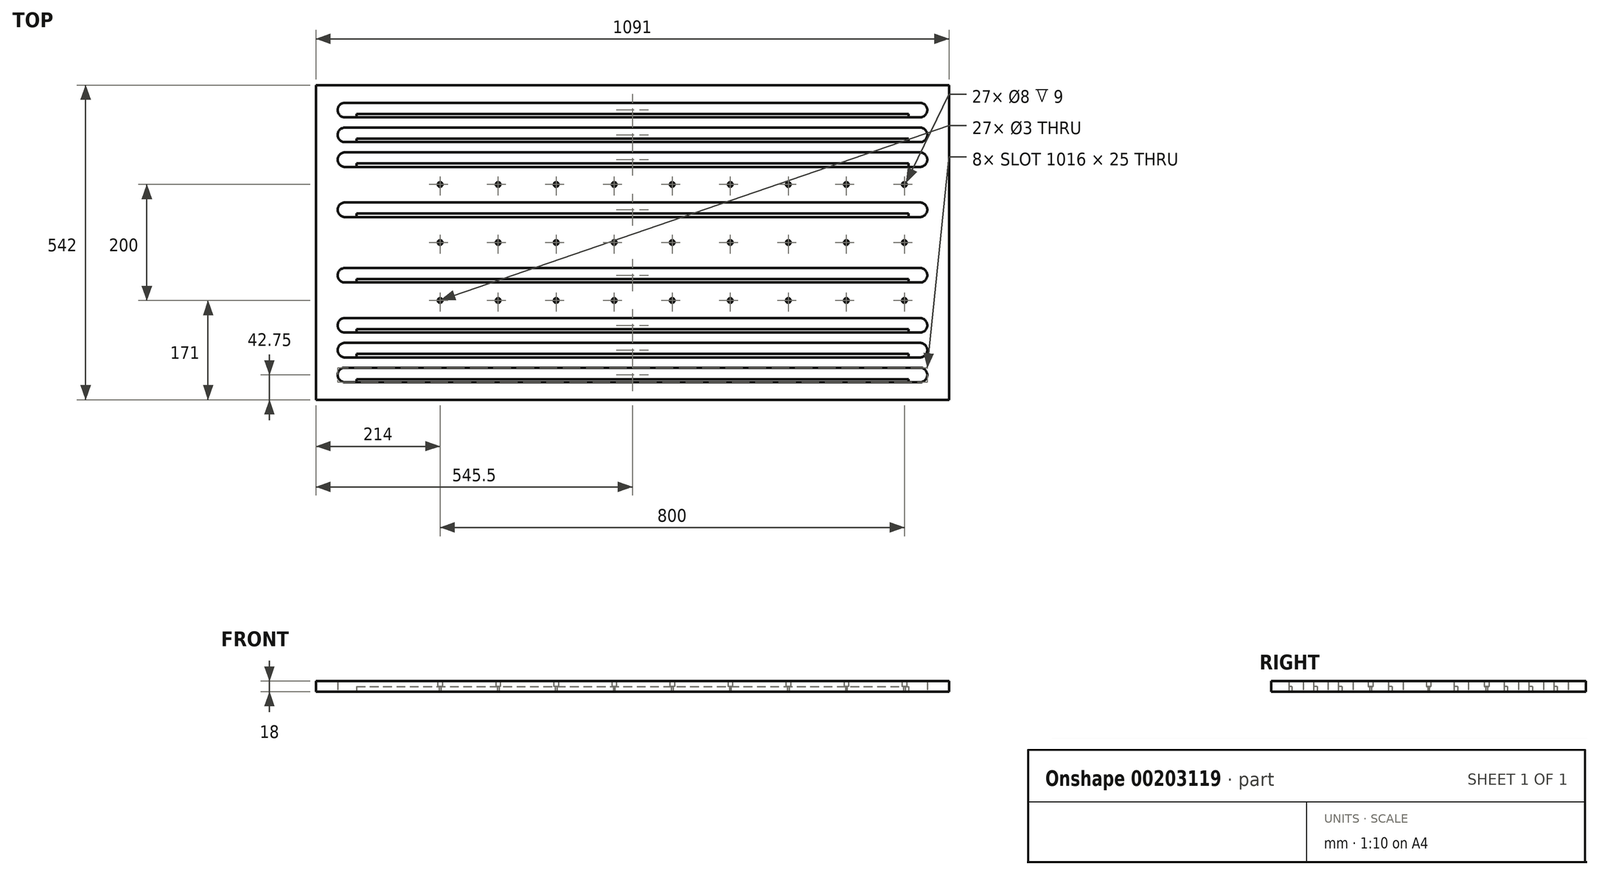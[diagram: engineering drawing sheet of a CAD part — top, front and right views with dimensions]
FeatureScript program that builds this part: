
annotation { "Feature Type Name" : "Feature", "Feature Type Description" : "" }
export const myFeature = defineFeature(function(context is Context, id is Id, definition is map)
    precondition{}
    {
        {
            var Q0;
            Q0=qCreatedBy(makeId("Top.planeOp"),FACE);
            var sketch = newSketch(context, id + "F0", { "sketchPlane" : qUnion([Q0])});
            skLineSegment(sketch, "E0.bottom", {"start": v(0, 0) * mm, "end": v(1091, 0) * mm});
            skLineSegment(sketch, "E0.top", {"start": v(0, 542) * mm, "end": v(1091, 542) * mm});
            skLineSegment(sketch, "E0.left", {"start": v(0, 0) * mm, "end": v(0, 542) * mm});
            skLineSegment(sketch, "E0.right", {"start": v(1091, 0) * mm, "end": v(1091, 542) * mm});
            skPoint(sketch, "E1", {"position": v(214, 171) * mm});
            skPoint(sketch, "E2", {"position": v(214, 271) * mm});
            skPoint(sketch, "E3", {"position": v(214, 371) * mm});
            skLineSegment(sketch, "E4", {"start": v(-315.3, 371) * mm, "end": v(-315.3, 271) * mm, "construction": true});
            skLineSegment(sketch, "E5", {"start": v(-315.3, 271) * mm, "end": v(-315.3, 171) * mm, "construction": true});
            skLineSegment(sketch, "E6", {"start": v(-315.3, 171) * mm, "end": v(-315.3, 0) * mm, "construction": true});
            skLineSegment(sketch, "E7", {"start": v(-315.3, 542) * mm, "end": v(-315.3, 371) * mm, "construction": true});
            skPoint(sketch, "E8", {"position": v(-315.3, 456.5) * mm});
            skPoint(sketch, "E9", {"position": v(-315.3, 327.44) * mm});
            skPoint(sketch, "E10", {"position": v(-315.3, 221) * mm});
            skPoint(sketch, "E11", {"position": v(-315.3, 85.5) * mm});
            skLineSegment(sketch, "E12", {"start": v(50, 327.44) * mm, "end": v(1041, 327.44) * mm, "construction": true});
            skLineSegment(sketch, "E13", {"start": v(50, 456.5) * mm, "end": v(1041, 456.5) * mm, "construction": true});
            skLineSegment(sketch, "E14", {"start": v(1046.67, 271) * mm, "end": v(1429.51, 271) * mm, "construction": true});
            skPoint(sketch, "E14.endSnap0", {"position": v(1091, 271) * mm});
            skLineSegment(sketch, "E15", {"start": v(-218.04, 542) * mm, "end": v(-218.04, 456.5) * mm, "construction": true});
            skPoint(sketch, "E16", {"position": v(-218.04, 499.25) * mm});
            skLineSegment(sketch, "E17", {"start": v(50, 499.25) * mm, "end": v(1041, 499.25) * mm, "construction": true});
            skLineSegment(sketch, "E18", {"start": v(-218.04, 456.5) * mm, "end": v(-218.04, 371) * mm, "construction": true});
            skPoint(sketch, "E19", {"position": v(-218.04, 413.75) * mm});
            skLineSegment(sketch, "E20", {"start": v(50, 413.75) * mm, "end": v(1041, 413.75) * mm, "construction": true});
            skLineSegment(sketch, "E21.MirrorCS", {"start": v(50, 42.75) * mm, "end": v(1041, 42.75) * mm, "construction": true});
            skLineSegment(sketch, "E22.MirrorCS", {"start": v(50, 85.5) * mm, "end": v(1041, 85.5) * mm, "construction": true});
            skLineSegment(sketch, "E23.MirrorCS", {"start": v(50, 128.25) * mm, "end": v(1041, 128.25) * mm, "construction": true});
            skLineSegment(sketch, "E24.MirrorCS", {"start": v(50, 214.56) * mm, "end": v(1041, 214.56) * mm, "construction": true});
            skSolve(sketch);
        }
        {
            var Q0;
            Q0=makeQuery(id+"F0.imprint","IMPRINT",FACE,{"disambiguationData":[TD([[makeQuery(id+"F0.imprint","IMPRINT",EDGE,{"derivedFrom":sQuery(id+"F0.wireOp",EDGE,"E0.bottom")}),1.0]])]});
            var sketch = newSketch(context, id + "F1", { "sketchPlane" : qUnion([Q0])});
            skLineSegment(sketch, "E25.bottom", {"start": v(0, 0) * mm, "end": v(1091, 0) * mm});
            skLineSegment(sketch, "E25.top", {"start": v(0, 542) * mm, "end": v(1091, 542) * mm});
            skLineSegment(sketch, "E25.left", {"start": v(0, 0) * mm, "end": v(0, 542) * mm});
            skLineSegment(sketch, "E25.right", {"start": v(1091, 0) * mm, "end": v(1091, 542) * mm});
            skLineSegment(sketch, "E26.JFx.JFx", {"start": v(50, 499.25) * mm, "end": v(1041, 499.25) * mm, "construction": true});
            skLineSegment(sketch, "E26.JFl.JFl", {"start": v(50, 456.5) * mm, "end": v(1041, 456.5) * mm, "construction": true});
            skLineSegment(sketch, "E26.JF5.JF5", {"start": v(50, 413.75) * mm, "end": v(1041, 413.75) * mm, "construction": true});
            skLineSegment(sketch, "E26.JFh.JFh", {"start": v(50, 327.44) * mm, "end": v(1041, 327.44) * mm, "construction": true});
            skLineSegment(sketch, "E26.KFJB.KFJB", {"start": v(50, 214.56) * mm, "end": v(1041, 214.56) * mm, "construction": true});
            skLineSegment(sketch, "E26.KFFB.KFFB", {"start": v(50, 128.25) * mm, "end": v(1041, 128.25) * mm, "construction": true});
            skLineSegment(sketch, "E26.KFBB.KFBB", {"start": v(50, 85.5) * mm, "end": v(1041, 85.5) * mm, "construction": true});
            skLineSegment(sketch, "E26.JF9.JF9", {"start": v(50, 42.75) * mm, "end": v(1041, 42.75) * mm, "construction": true});
            skArc(sketch, "E26.0.startCap", {"start": v(50, 486.75) * mm, "mid": v(37.5, 499.25) * mm, "end": v(50, 511.75) * mm});
            skArc(sketch, "E26.0.endCap", {"start": v(1041, 511.75) * mm, "mid": v(1053.5, 499.25) * mm, "end": v(1041, 486.75) * mm});
            skLineSegment(sketch, "E26.0.left", {"start": v(50, 511.75) * mm, "end": v(1041, 511.75) * mm});
            skLineSegment(sketch, "E26.0.right", {"start": v(50, 486.75) * mm, "end": v(1041, 486.75) * mm});
            skArc(sketch, "E26.1.startCap", {"start": v(50, 444) * mm, "mid": v(37.5, 456.5) * mm, "end": v(50, 469) * mm});
            skArc(sketch, "E26.1.endCap", {"start": v(1041, 469) * mm, "mid": v(1053.5, 456.5) * mm, "end": v(1041, 444) * mm});
            skLineSegment(sketch, "E26.1.left", {"start": v(50, 469) * mm, "end": v(1041, 469) * mm});
            skLineSegment(sketch, "E26.1.right", {"start": v(50, 444) * mm, "end": v(1041, 444) * mm});
            skArc(sketch, "E26.2.startCap", {"start": v(50, 401.25) * mm, "mid": v(37.5, 413.75) * mm, "end": v(50, 426.25) * mm});
            skArc(sketch, "E26.2.endCap", {"start": v(1041, 426.25) * mm, "mid": v(1053.5, 413.75) * mm, "end": v(1041, 401.25) * mm});
            skLineSegment(sketch, "E26.2.left", {"start": v(50, 426.25) * mm, "end": v(1041, 426.25) * mm});
            skLineSegment(sketch, "E26.2.right", {"start": v(50, 401.25) * mm, "end": v(1041, 401.25) * mm});
            skArc(sketch, "E26.3.startCap", {"start": v(50, 314.94) * mm, "mid": v(37.5, 327.44) * mm, "end": v(50, 339.94) * mm});
            skArc(sketch, "E26.3.endCap", {"start": v(1041, 339.94) * mm, "mid": v(1053.5, 327.44) * mm, "end": v(1041, 314.94) * mm});
            skLineSegment(sketch, "E26.3.left", {"start": v(50, 339.94) * mm, "end": v(1041, 339.94) * mm});
            skLineSegment(sketch, "E26.3.right", {"start": v(50, 314.94) * mm, "end": v(1041, 314.94) * mm});
            skArc(sketch, "E26.4.startCap", {"start": v(50, 202.06) * mm, "mid": v(37.5, 214.56) * mm, "end": v(50, 227.06) * mm});
            skArc(sketch, "E26.4.endCap", {"start": v(1041, 227.06) * mm, "mid": v(1053.5, 214.56) * mm, "end": v(1041, 202.06) * mm});
            skLineSegment(sketch, "E26.4.left", {"start": v(50, 227.06) * mm, "end": v(1041, 227.06) * mm});
            skLineSegment(sketch, "E26.4.right", {"start": v(50, 202.06) * mm, "end": v(1041, 202.06) * mm});
            skArc(sketch, "E26.5.startCap", {"start": v(50, 115.75) * mm, "mid": v(37.5, 128.25) * mm, "end": v(50, 140.75) * mm});
            skArc(sketch, "E26.5.endCap", {"start": v(1041, 140.75) * mm, "mid": v(1053.5, 128.25) * mm, "end": v(1041, 115.75) * mm});
            skLineSegment(sketch, "E26.5.left", {"start": v(50, 140.75) * mm, "end": v(1041, 140.75) * mm});
            skLineSegment(sketch, "E26.5.right", {"start": v(50, 115.75) * mm, "end": v(1041, 115.75) * mm});
            skArc(sketch, "E26.6.startCap", {"start": v(50, 73) * mm, "mid": v(37.5, 85.5) * mm, "end": v(50, 98) * mm});
            skArc(sketch, "E26.6.endCap", {"start": v(1041, 98) * mm, "mid": v(1053.5, 85.5) * mm, "end": v(1041, 73) * mm});
            skLineSegment(sketch, "E26.6.left", {"start": v(50, 98) * mm, "end": v(1041, 98) * mm});
            skLineSegment(sketch, "E26.6.right", {"start": v(50, 73) * mm, "end": v(1041, 73) * mm});
            skArc(sketch, "E26.7.startCap", {"start": v(50, 30.25) * mm, "mid": v(37.5, 42.75) * mm, "end": v(50, 55.25) * mm});
            skArc(sketch, "E26.7.endCap", {"start": v(1041, 55.25) * mm, "mid": v(1053.5, 42.75) * mm, "end": v(1041, 30.25) * mm});
            skLineSegment(sketch, "E26.7.left", {"start": v(50, 55.25) * mm, "end": v(1041, 55.25) * mm});
            skLineSegment(sketch, "E26.7.right", {"start": v(50, 30.25) * mm, "end": v(1041, 30.25) * mm});
            skPoint(sketch, "E27", {"position": v(545.5, 511.75) * mm});
            skLineSegment(sketch, "E28.bottom", {"start": v(70, 511.75) * mm, "end": v(1021, 511.75) * mm});
            skLineSegment(sketch, "E28.top", {"start": v(70, 505.75) * mm, "end": v(1021, 505.75) * mm});
            skLineSegment(sketch, "E28.left", {"start": v(70, 511.75) * mm, "end": v(70, 505.75) * mm});
            skLineSegment(sketch, "E28.right", {"start": v(1021, 511.75) * mm, "end": v(1021, 505.75) * mm});
            skLineSegment(sketch, "E29.bottom", {"start": v(70, 492.75) * mm, "end": v(1021, 492.75) * mm});
            skLineSegment(sketch, "E29.top", {"start": v(70, 486.75) * mm, "end": v(1021, 486.75) * mm});
            skLineSegment(sketch, "E29.left", {"start": v(70, 492.75) * mm, "end": v(70, 486.75) * mm});
            skLineSegment(sketch, "E29.right", {"start": v(1021, 492.75) * mm, "end": v(1021, 486.75) * mm});
            skLineSegment(sketch, "E30.bottom", {"start": v(70, 98) * mm, "end": v(1021, 98) * mm});
            skLineSegment(sketch, "E30.top", {"start": v(70, 92) * mm, "end": v(1021, 92) * mm});
            skLineSegment(sketch, "E30.left", {"start": v(1021, 98) * mm, "end": v(1021, 92) * mm});
            skLineSegment(sketch, "E30.right", {"start": v(70, 98) * mm, "end": v(70, 92) * mm});
            skPoint(sketch, "E31", {"position": v(545.5, 98) * mm});
            skLineSegment(sketch, "E32.bottom", {"start": v(70, 79) * mm, "end": v(1021, 79) * mm});
            skLineSegment(sketch, "E32.top", {"start": v(70, 73) * mm, "end": v(1021, 73) * mm});
            skLineSegment(sketch, "E32.left", {"start": v(1021, 79) * mm, "end": v(1021, 73) * mm});
            skLineSegment(sketch, "E32.right", {"start": v(70, 79) * mm, "end": v(70, 73) * mm});
            skLineSegment(sketch, "E33.bottom", {"start": v(70, 426.25) * mm, "end": v(1021, 426.25) * mm});
            skLineSegment(sketch, "E33.top", {"start": v(70, 420.25) * mm, "end": v(1021, 420.25) * mm});
            skLineSegment(sketch, "E33.left", {"start": v(1021, 426.25) * mm, "end": v(1021, 420.25) * mm});
            skLineSegment(sketch, "E33.right", {"start": v(70, 426.25) * mm, "end": v(70, 420.25) * mm});
            skPoint(sketch, "E34", {"position": v(545.5, 426.25) * mm});
            skLineSegment(sketch, "E35.bottom", {"start": v(70, 407.25) * mm, "end": v(1021, 407.25) * mm});
            skLineSegment(sketch, "E35.top", {"start": v(70, 401.25) * mm, "end": v(1021, 401.25) * mm});
            skLineSegment(sketch, "E35.left", {"start": v(1021, 407.25) * mm, "end": v(1021, 401.25) * mm});
            skLineSegment(sketch, "E35.right", {"start": v(70, 407.25) * mm, "end": v(70, 401.25) * mm});
            skLineSegment(sketch, "E36.bottom", {"start": v(70, 469) * mm, "end": v(1021, 469) * mm});
            skLineSegment(sketch, "E36.top", {"start": v(70, 463) * mm, "end": v(1021, 463) * mm});
            skLineSegment(sketch, "E36.left", {"start": v(1021, 469) * mm, "end": v(1021, 463) * mm});
            skLineSegment(sketch, "E36.right", {"start": v(70, 469) * mm, "end": v(70, 463) * mm});
            skPoint(sketch, "E37", {"position": v(545.5, 469) * mm});
            skLineSegment(sketch, "E38.bottom", {"start": v(70, 450) * mm, "end": v(1021, 450) * mm});
            skLineSegment(sketch, "E38.top", {"start": v(70, 444) * mm, "end": v(1021, 444) * mm});
            skLineSegment(sketch, "E38.left", {"start": v(1021, 450) * mm, "end": v(1021, 444) * mm});
            skLineSegment(sketch, "E38.right", {"start": v(70, 450) * mm, "end": v(70, 444) * mm});
            skPoint(sketch, "E39", {"position": v(545.5, 339.94) * mm});
            skPoint(sketch, "E40", {"position": v(545.5, 227.06) * mm});
            skPoint(sketch, "E41", {"position": v(545.5, 140.75) * mm});
            skPoint(sketch, "E42", {"position": v(545.5, 55.25) * mm});
            skLineSegment(sketch, "E43.bottom", {"start": v(70, 140.75) * mm, "end": v(1021, 140.75) * mm});
            skLineSegment(sketch, "E43.top", {"start": v(70, 134.75) * mm, "end": v(1021, 134.75) * mm});
            skLineSegment(sketch, "E43.left", {"start": v(70, 140.75) * mm, "end": v(70, 134.75) * mm});
            skLineSegment(sketch, "E43.right", {"start": v(1021, 140.75) * mm, "end": v(1021, 134.75) * mm});
            skLineSegment(sketch, "E44.bottom", {"start": v(70, 121.75) * mm, "end": v(1021, 121.75) * mm});
            skLineSegment(sketch, "E44.top", {"start": v(70, 115.75) * mm, "end": v(1021, 115.75) * mm});
            skLineSegment(sketch, "E44.left", {"start": v(70, 121.75) * mm, "end": v(70, 115.75) * mm});
            skLineSegment(sketch, "E44.right", {"start": v(1021, 121.75) * mm, "end": v(1021, 115.75) * mm});
            skLineSegment(sketch, "E45.bottom", {"start": v(70, 55.25) * mm, "end": v(1021, 55.25) * mm});
            skLineSegment(sketch, "E45.top", {"start": v(70, 50.25) * mm, "end": v(1021, 50.25) * mm});
            skLineSegment(sketch, "E45.left", {"start": v(70, 55.25) * mm, "end": v(70, 50.25) * mm});
            skLineSegment(sketch, "E45.right", {"start": v(1021, 55.25) * mm, "end": v(1021, 50.25) * mm});
            skLineSegment(sketch, "E46.bottom", {"start": v(70, 35.25) * mm, "end": v(1021, 35.25) * mm});
            skLineSegment(sketch, "E46.top", {"start": v(70, 30.25) * mm, "end": v(1021, 30.25) * mm});
            skLineSegment(sketch, "E46.left", {"start": v(70, 35.25) * mm, "end": v(70, 30.25) * mm});
            skLineSegment(sketch, "E46.right", {"start": v(1021, 35.25) * mm, "end": v(1021, 30.25) * mm});
            skLineSegment(sketch, "E47.bottom", {"start": v(70, 227.06) * mm, "end": v(1021, 227.06) * mm});
            skLineSegment(sketch, "E47.top", {"start": v(70, 221.06) * mm, "end": v(1021, 221.06) * mm});
            skLineSegment(sketch, "E47.left", {"start": v(70, 227.06) * mm, "end": v(70, 221.06) * mm});
            skLineSegment(sketch, "E47.right", {"start": v(1021, 227.06) * mm, "end": v(1021, 221.06) * mm});
            skLineSegment(sketch, "E48.bottom", {"start": v(70, 208.06) * mm, "end": v(1021, 208.06) * mm});
            skLineSegment(sketch, "E48.top", {"start": v(70, 202.06) * mm, "end": v(1021, 202.06) * mm});
            skLineSegment(sketch, "E48.left", {"start": v(70, 208.06) * mm, "end": v(70, 202.06) * mm});
            skLineSegment(sketch, "E48.right", {"start": v(1021, 208.06) * mm, "end": v(1021, 202.06) * mm});
            skPoint(sketch, "E49", {"position": v(545.5, 30.25) * mm});
            skLineSegment(sketch, "E50.bottom", {"start": v(70, 339.94) * mm, "end": v(1021, 339.94) * mm});
            skLineSegment(sketch, "E50.top", {"start": v(70, 333.94) * mm, "end": v(1021, 333.94) * mm});
            skLineSegment(sketch, "E50.left", {"start": v(70, 339.94) * mm, "end": v(70, 333.94) * mm});
            skLineSegment(sketch, "E50.right", {"start": v(1021, 339.94) * mm, "end": v(1021, 333.94) * mm});
            skLineSegment(sketch, "E51.bottom", {"start": v(70, 320.94) * mm, "end": v(1021, 320.94) * mm});
            skLineSegment(sketch, "E51.top", {"start": v(70, 314.94) * mm, "end": v(1021, 314.94) * mm});
            skLineSegment(sketch, "E51.left", {"start": v(70, 320.94) * mm, "end": v(70, 314.94) * mm});
            skLineSegment(sketch, "E51.right", {"start": v(1021, 320.94) * mm, "end": v(1021, 314.94) * mm});
            skPoint(sketch, "E52", {"position": v(545.5, 214.56) * mm});
            skCircle(sketch, "E53", {"center": v(214, 171) * mm, "radius": 4 * mm});
            skCircle(sketch, "E54", {"center": v(214, 171) * mm, "radius": 1.5 * mm});
            skCircle(sketch, "E55.0.1.0", {"center": v(214, 271) * mm, "radius": 4 * mm});
            skCircle(sketch, "E55.0.1.1", {"center": v(214, 271) * mm, "radius": 1.5 * mm});
            skCircle(sketch, "E55.0.2.0", {"center": v(214, 371) * mm, "radius": 4 * mm});
            skCircle(sketch, "E55.0.2.1", {"center": v(214, 371) * mm, "radius": 1.5 * mm});
            skCircle(sketch, "E55.1.0.0", {"center": v(314, 171) * mm, "radius": 4 * mm});
            skCircle(sketch, "E55.1.0.1", {"center": v(314, 171) * mm, "radius": 1.5 * mm});
            skCircle(sketch, "E55.1.1.0", {"center": v(314, 271) * mm, "radius": 4 * mm});
            skCircle(sketch, "E55.1.1.1", {"center": v(314, 271) * mm, "radius": 1.5 * mm});
            skCircle(sketch, "E55.1.2.0", {"center": v(314, 371) * mm, "radius": 4 * mm});
            skCircle(sketch, "E55.1.2.1", {"center": v(314, 371) * mm, "radius": 1.5 * mm});
            skCircle(sketch, "E55.2.0.0", {"center": v(414, 171) * mm, "radius": 4 * mm});
            skCircle(sketch, "E55.2.0.1", {"center": v(414, 171) * mm, "radius": 1.5 * mm});
            skCircle(sketch, "E55.2.1.0", {"center": v(414, 271) * mm, "radius": 4 * mm});
            skCircle(sketch, "E55.2.1.1", {"center": v(414, 271) * mm, "radius": 1.5 * mm});
            skCircle(sketch, "E55.2.2.0", {"center": v(414, 371) * mm, "radius": 4 * mm});
            skCircle(sketch, "E55.2.2.1", {"center": v(414, 371) * mm, "radius": 1.5 * mm});
            skCircle(sketch, "E55.3.0.0", {"center": v(514, 171) * mm, "radius": 4 * mm});
            skCircle(sketch, "E55.3.0.1", {"center": v(514, 171) * mm, "radius": 1.5 * mm});
            skCircle(sketch, "E55.3.1.0", {"center": v(514, 271) * mm, "radius": 4 * mm});
            skCircle(sketch, "E55.3.1.1", {"center": v(514, 271) * mm, "radius": 1.5 * mm});
            skCircle(sketch, "E55.3.2.0", {"center": v(514, 371) * mm, "radius": 4 * mm});
            skCircle(sketch, "E55.3.2.1", {"center": v(514, 371) * mm, "radius": 1.5 * mm});
            skCircle(sketch, "E55.4.0.0", {"center": v(614, 171) * mm, "radius": 4 * mm});
            skCircle(sketch, "E55.4.0.1", {"center": v(614, 171) * mm, "radius": 1.5 * mm});
            skCircle(sketch, "E55.4.1.0", {"center": v(614, 271) * mm, "radius": 4 * mm});
            skCircle(sketch, "E55.4.1.1", {"center": v(614, 271) * mm, "radius": 1.5 * mm});
            skCircle(sketch, "E55.4.2.0", {"center": v(614, 371) * mm, "radius": 4 * mm});
            skCircle(sketch, "E55.4.2.1", {"center": v(614, 371) * mm, "radius": 1.5 * mm});
            skCircle(sketch, "E55.5.0.0", {"center": v(714, 171) * mm, "radius": 4 * mm});
            skCircle(sketch, "E55.5.0.1", {"center": v(714, 171) * mm, "radius": 1.5 * mm});
            skCircle(sketch, "E55.5.1.0", {"center": v(714, 271) * mm, "radius": 4 * mm});
            skCircle(sketch, "E55.5.1.1", {"center": v(714, 271) * mm, "radius": 1.5 * mm});
            skCircle(sketch, "E55.5.2.0", {"center": v(714, 371) * mm, "radius": 4 * mm});
            skCircle(sketch, "E55.5.2.1", {"center": v(714, 371) * mm, "radius": 1.5 * mm});
            skCircle(sketch, "E55.6.0.0", {"center": v(814, 171) * mm, "radius": 4 * mm});
            skCircle(sketch, "E55.6.0.1", {"center": v(814, 171) * mm, "radius": 1.5 * mm});
            skCircle(sketch, "E55.6.1.0", {"center": v(814, 271) * mm, "radius": 4 * mm});
            skCircle(sketch, "E55.6.1.1", {"center": v(814, 271) * mm, "radius": 1.5 * mm});
            skCircle(sketch, "E55.6.2.0", {"center": v(814, 371) * mm, "radius": 4 * mm});
            skCircle(sketch, "E55.6.2.1", {"center": v(814, 371) * mm, "radius": 1.5 * mm});
            skCircle(sketch, "E55.7.0.0", {"center": v(914, 171) * mm, "radius": 4 * mm});
            skCircle(sketch, "E55.7.0.1", {"center": v(914, 171) * mm, "radius": 1.5 * mm});
            skCircle(sketch, "E55.7.1.0", {"center": v(914, 271) * mm, "radius": 4 * mm});
            skCircle(sketch, "E55.7.1.1", {"center": v(914, 271) * mm, "radius": 1.5 * mm});
            skCircle(sketch, "E55.7.2.0", {"center": v(914, 371) * mm, "radius": 4 * mm});
            skCircle(sketch, "E55.7.2.1", {"center": v(914, 371) * mm, "radius": 1.5 * mm});
            skCircle(sketch, "E55.8.0.0", {"center": v(1014, 171) * mm, "radius": 4 * mm});
            skCircle(sketch, "E55.8.0.1", {"center": v(1014, 171) * mm, "radius": 1.5 * mm});
            skCircle(sketch, "E55.8.1.0", {"center": v(1014, 271) * mm, "radius": 4 * mm});
            skCircle(sketch, "E55.8.1.1", {"center": v(1014, 271) * mm, "radius": 1.5 * mm});
            skCircle(sketch, "E55.8.2.0", {"center": v(1014, 371) * mm, "radius": 4 * mm});
            skCircle(sketch, "E55.8.2.1", {"center": v(1014, 371) * mm, "radius": 1.5 * mm});
            skLineSegment(sketch, "E55.direction1", {"start": v(214, 171) * mm, "end": v(314, 171) * mm, "construction": true});
            skLineSegment(sketch, "E55.direction2", {"start": v(214, 171) * mm, "end": v(214, 271) * mm, "construction": true});
            skSolve(sketch);
        }
        {
            var Q0;
            Q0=makeQuery(id+"F1.imprint","IMPRINT",FACE,{"disambiguationData":[TD([[makeQuery(id+"F1.imprint","IMPRINT",EDGE,{"derivedFrom":sQuery(id+"F1.wireOp",EDGE,"E25.bottom")}),1.0]])]});
            extrude(context, id + "F2", {"entities" : qUnion([Q0]), "depth" : 18 * mm});
        }
        {
            var Q0;
            Q0=makeQuery(id+"F1.imprint","IMPRINT",FACE,{"disambiguationData":[TD([[makeQuery(id+"F1.imprint","IMPRINT",EDGE,{"derivedFrom":sQuery(id+"F1.wireOp",EDGE,"E55.2.2.0")}),1.0]])]});
            var Q1;
            Q1=makeQuery(id+"F1.imprint","IMPRINT",FACE,{"disambiguationData":[TD([[makeQuery(id+"F1.imprint","IMPRINT",EDGE,{"derivedFrom":sQuery(id+"F1.wireOp",EDGE,"E55.1.2.0")}),1.0]])]});
            var Q2;
            Q2=makeQuery(id+"F1.imprint","IMPRINT",FACE,{"disambiguationData":[TD([[makeQuery(id+"F1.imprint","IMPRINT",EDGE,{"derivedFrom":sQuery(id+"F1.wireOp",EDGE,"E55.0.2.0")}),1.0]])]});
            var Q3;
            Q3=makeQuery(id+"F1.imprint","IMPRINT",FACE,{"disambiguationData":[TD([[makeQuery(id+"F1.imprint","IMPRINT",EDGE,{"derivedFrom":sQuery(id+"F1.wireOp",EDGE,"E55.0.1.0")}),1.0]])]});
            var Q4;
            Q4=makeQuery(id+"F1.imprint","IMPRINT",FACE,{"disambiguationData":[TD([[makeQuery(id+"F1.imprint","IMPRINT",EDGE,{"derivedFrom":sQuery(id+"F1.wireOp",EDGE,"E55.1.1.0")}),1.0]])]});
            var Q5;
            Q5=makeQuery(id+"F1.imprint","IMPRINT",FACE,{"disambiguationData":[TD([[makeQuery(id+"F1.imprint","IMPRINT",EDGE,{"derivedFrom":sQuery(id+"F1.wireOp",EDGE,"E55.2.1.0")}),1.0]])]});
            var Q6;
            Q6=makeQuery(id+"F1.imprint","IMPRINT",FACE,{"disambiguationData":[TD([[makeQuery(id+"F1.imprint","IMPRINT",EDGE,{"derivedFrom":sQuery(id+"F1.wireOp",EDGE,"E55.3.1.0")}),1.0]])]});
            var Q7;
            Q7=makeQuery(id+"F1.imprint","IMPRINT",FACE,{"disambiguationData":[TD([[makeQuery(id+"F1.imprint","IMPRINT",EDGE,{"derivedFrom":sQuery(id+"F1.wireOp",EDGE,"E55.4.1.0")}),1.0]])]});
            var Q8;
            Q8=makeQuery(id+"F1.imprint","IMPRINT",FACE,{"disambiguationData":[TD([[makeQuery(id+"F1.imprint","IMPRINT",EDGE,{"derivedFrom":sQuery(id+"F1.wireOp",EDGE,"E55.5.1.0")}),1.0]])]});
            var Q9;
            Q9=makeQuery(id+"F1.imprint","IMPRINT",FACE,{"disambiguationData":[TD([[makeQuery(id+"F1.imprint","IMPRINT",EDGE,{"derivedFrom":sQuery(id+"F1.wireOp",EDGE,"E55.6.1.0")}),1.0]])]});
            var Q10;
            Q10=makeQuery(id+"F1.imprint","IMPRINT",FACE,{"disambiguationData":[TD([[makeQuery(id+"F1.imprint","IMPRINT",EDGE,{"derivedFrom":sQuery(id+"F1.wireOp",EDGE,"E55.7.1.0")}),1.0]])]});
            var Q11;
            Q11=makeQuery(id+"F1.imprint","IMPRINT",FACE,{"disambiguationData":[TD([[makeQuery(id+"F1.imprint","IMPRINT",EDGE,{"derivedFrom":sQuery(id+"F1.wireOp",EDGE,"E55.8.1.0")}),1.0]])]});
            var Q12;
            Q12=makeQuery(id+"F1.imprint","IMPRINT",FACE,{"disambiguationData":[TD([[makeQuery(id+"F1.imprint","IMPRINT",EDGE,{"derivedFrom":sQuery(id+"F1.wireOp",EDGE,"E55.8.0.0")}),1.0]])]});
            var Q13;
            Q13=makeQuery(id+"F1.imprint","IMPRINT",FACE,{"disambiguationData":[TD([[makeQuery(id+"F1.imprint","IMPRINT",EDGE,{"derivedFrom":sQuery(id+"F1.wireOp",EDGE,"E55.7.0.0")}),1.0]])]});
            var Q14;
            Q14=makeQuery(id+"F1.imprint","IMPRINT",FACE,{"disambiguationData":[TD([[makeQuery(id+"F1.imprint","IMPRINT",EDGE,{"derivedFrom":sQuery(id+"F1.wireOp",EDGE,"E55.6.0.0")}),1.0]])]});
            var Q15;
            Q15=makeQuery(id+"F1.imprint","IMPRINT",FACE,{"disambiguationData":[TD([[makeQuery(id+"F1.imprint","IMPRINT",EDGE,{"derivedFrom":sQuery(id+"F1.wireOp",EDGE,"E55.5.0.0")}),1.0]])]});
            var Q16;
            Q16=makeQuery(id+"F1.imprint","IMPRINT",FACE,{"disambiguationData":[TD([[makeQuery(id+"F1.imprint","IMPRINT",EDGE,{"derivedFrom":sQuery(id+"F1.wireOp",EDGE,"E55.4.0.0")}),1.0]])]});
            var Q17;
            Q17=makeQuery(id+"F1.imprint","IMPRINT",FACE,{"disambiguationData":[TD([[makeQuery(id+"F1.imprint","IMPRINT",EDGE,{"derivedFrom":sQuery(id+"F1.wireOp",EDGE,"E55.3.0.0")}),1.0]])]});
            var Q18;
            Q18=makeQuery(id+"F1.imprint","IMPRINT",FACE,{"disambiguationData":[TD([[makeQuery(id+"F1.imprint","IMPRINT",EDGE,{"derivedFrom":sQuery(id+"F1.wireOp",EDGE,"E55.2.0.0")}),1.0]])]});
            var Q19;
            Q19=makeQuery(id+"F1.imprint","IMPRINT",FACE,{"disambiguationData":[TD([[makeQuery(id+"F1.imprint","IMPRINT",EDGE,{"derivedFrom":sQuery(id+"F1.wireOp",EDGE,"E55.1.0.0")}),1.0]])]});
            var Q20;
            Q20=makeQuery(id+"F1.imprint","IMPRINT",FACE,{"disambiguationData":[TD([[makeQuery(id+"F1.imprint","IMPRINT",EDGE,{"derivedFrom":sQuery(id+"F1.wireOp",EDGE,"E53")}),1.0]])]});
            var Q21;
            Q21=makeQuery(id+"F1.imprint","IMPRINT",FACE,{"disambiguationData":[TD([[makeQuery(id+"F1.imprint","IMPRINT",EDGE,{"derivedFrom":sQuery(id+"F1.wireOp",EDGE,"E55.8.2.0")}),1.0]])]});
            var Q22;
            Q22=makeQuery(id+"F1.imprint","IMPRINT",FACE,{"disambiguationData":[TD([[makeQuery(id+"F1.imprint","IMPRINT",EDGE,{"derivedFrom":sQuery(id+"F1.wireOp",EDGE,"E55.7.2.0")}),1.0]])]});
            var Q23;
            Q23=makeQuery(id+"F1.imprint","IMPRINT",FACE,{"disambiguationData":[TD([[makeQuery(id+"F1.imprint","IMPRINT",EDGE,{"derivedFrom":sQuery(id+"F1.wireOp",EDGE,"E55.6.2.0")}),1.0]])]});
            var Q24;
            Q24=makeQuery(id+"F1.imprint","IMPRINT",FACE,{"disambiguationData":[TD([[makeQuery(id+"F1.imprint","IMPRINT",EDGE,{"derivedFrom":sQuery(id+"F1.wireOp",EDGE,"E55.5.2.0")}),1.0]])]});
            var Q25;
            Q25=makeQuery(id+"F1.imprint","IMPRINT",FACE,{"disambiguationData":[TD([[makeQuery(id+"F1.imprint","IMPRINT",EDGE,{"derivedFrom":sQuery(id+"F1.wireOp",EDGE,"E55.4.2.0")}),1.0]])]});
            var Q26;
            Q26=makeQuery(id+"F1.imprint","IMPRINT",FACE,{"disambiguationData":[TD([[makeQuery(id+"F1.imprint","IMPRINT",EDGE,{"derivedFrom":sQuery(id+"F1.wireOp",EDGE,"E55.3.2.0")}),1.0]])]});
            var Q27;
            Q27=makeQuery(id+"F1.imprint","IMPRINT",FACE,{"disambiguationData":[TD([[makeQuery(id+"F1.imprint","IMPRINT",EDGE,{"derivedFrom":sQuery(id+"F1.wireOp",EDGE,"E28.bottom")}),-1.0]])]});
            var Q28;
            Q28=makeQuery(id+"F1.imprint","IMPRINT",FACE,{"disambiguationData":[TD([[makeQuery(id+"F1.imprint","IMPRINT",EDGE,{"derivedFrom":sQuery(id+"F1.wireOp",EDGE,"E29.bottom")}),-1.0]])]});
            var Q29;
            Q29=makeQuery(id+"F1.imprint","IMPRINT",FACE,{"disambiguationData":[TD([[makeQuery(id+"F1.imprint","IMPRINT",EDGE,{"derivedFrom":sQuery(id+"F1.wireOp",EDGE,"E36.bottom")}),-1.0]])]});
            var Q30;
            Q30=makeQuery(id+"F1.imprint","IMPRINT",FACE,{"disambiguationData":[TD([[makeQuery(id+"F1.imprint","IMPRINT",EDGE,{"derivedFrom":sQuery(id+"F1.wireOp",EDGE,"E38.bottom")}),-1.0]])]});
            var Q31;
            Q31=makeQuery(id+"F1.imprint","IMPRINT",FACE,{"disambiguationData":[TD([[makeQuery(id+"F1.imprint","IMPRINT",EDGE,{"derivedFrom":sQuery(id+"F1.wireOp",EDGE,"E33.bottom")}),-1.0]])]});
            var Q32;
            Q32=makeQuery(id+"F1.imprint","IMPRINT",FACE,{"disambiguationData":[TD([[makeQuery(id+"F1.imprint","IMPRINT",EDGE,{"derivedFrom":sQuery(id+"F1.wireOp",EDGE,"E35.bottom")}),-1.0]])]});
            var Q33;
            Q33=makeQuery(id+"F1.imprint","IMPRINT",FACE,{"disambiguationData":[TD([[makeQuery(id+"F1.imprint","IMPRINT",EDGE,{"derivedFrom":sQuery(id+"F1.wireOp",EDGE,"E50.bottom")}),-1.0]])]});
            var Q34;
            Q34=makeQuery(id+"F1.imprint","IMPRINT",FACE,{"disambiguationData":[TD([[makeQuery(id+"F1.imprint","IMPRINT",EDGE,{"derivedFrom":sQuery(id+"F1.wireOp",EDGE,"E51.bottom")}),-1.0]])]});
            var Q35;
            Q35=makeQuery(id+"F1.imprint","IMPRINT",FACE,{"disambiguationData":[TD([[makeQuery(id+"F1.imprint","IMPRINT",EDGE,{"derivedFrom":sQuery(id+"F1.wireOp",EDGE,"E47.bottom")}),-1.0]])]});
            var Q36;
            Q36=makeQuery(id+"F1.imprint","IMPRINT",FACE,{"disambiguationData":[TD([[makeQuery(id+"F1.imprint","IMPRINT",EDGE,{"derivedFrom":sQuery(id+"F1.wireOp",EDGE,"E48.bottom")}),-1.0]])]});
            var Q37;
            Q37=makeQuery(id+"F1.imprint","IMPRINT",FACE,{"disambiguationData":[TD([[makeQuery(id+"F1.imprint","IMPRINT",EDGE,{"derivedFrom":sQuery(id+"F1.wireOp",EDGE,"E43.bottom")}),-1.0]])]});
            var Q38;
            Q38=makeQuery(id+"F1.imprint","IMPRINT",FACE,{"disambiguationData":[TD([[makeQuery(id+"F1.imprint","IMPRINT",EDGE,{"derivedFrom":sQuery(id+"F1.wireOp",EDGE,"E44.bottom")}),-1.0]])]});
            var Q39;
            Q39=makeQuery(id+"F1.imprint","IMPRINT",FACE,{"disambiguationData":[TD([[makeQuery(id+"F1.imprint","IMPRINT",EDGE,{"derivedFrom":sQuery(id+"F1.wireOp",EDGE,"E30.bottom")}),-1.0]])]});
            var Q40;
            Q40=makeQuery(id+"F1.imprint","IMPRINT",FACE,{"disambiguationData":[TD([[makeQuery(id+"F1.imprint","IMPRINT",EDGE,{"derivedFrom":sQuery(id+"F1.wireOp",EDGE,"E32.bottom")}),-1.0]])]});
            var Q41;
            Q41=makeQuery(id+"F1.imprint","IMPRINT",FACE,{"disambiguationData":[TD([[makeQuery(id+"F1.imprint","IMPRINT",EDGE,{"derivedFrom":sQuery(id+"F1.wireOp",EDGE,"E45.bottom")}),-1.0]])]});
            var Q42;
            Q42=makeQuery(id+"F1.imprint","IMPRINT",FACE,{"disambiguationData":[TD([[makeQuery(id+"F1.imprint","IMPRINT",EDGE,{"derivedFrom":sQuery(id+"F1.wireOp",EDGE,"E46.bottom")}),-1.0]])]});
            extrude(context, id + "F3", {"entities" : qUnion([Q0, Q1, Q2, Q3, Q4, Q5, Q6, Q7, Q8, Q9, Q10, Q11, Q12, Q13, Q14, Q15, Q16, Q17, Q18, Q19, Q20, Q21, Q22, Q23, Q24, Q25, Q26, Q27, Q28, Q29, Q30, Q31, Q32, Q33, Q34, Q35, Q36, Q37, Q38, Q39, Q40, Q41, Q42]), "operationType" : NewBodyOperationType.ADD, "depth" : 9 * mm});
        }
    });
